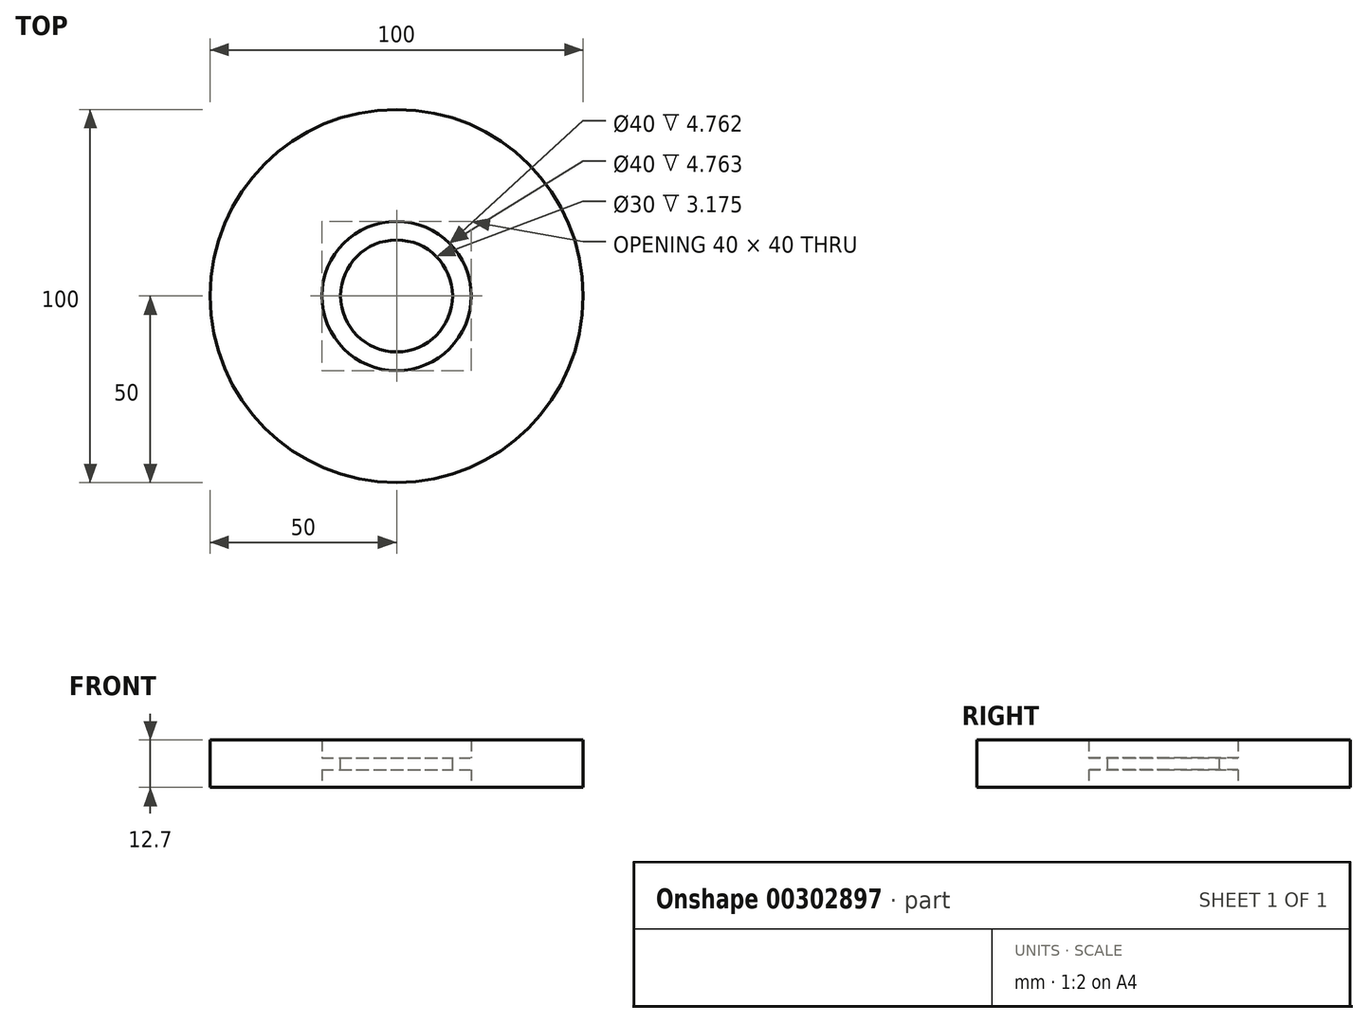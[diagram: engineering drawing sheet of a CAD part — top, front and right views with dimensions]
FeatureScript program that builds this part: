
annotation { "Feature Type Name" : "Feature", "Feature Type Description" : "" }
export const myFeature = defineFeature(function(context is Context, id is Id, definition is map)
    precondition{}
    {
        {
            var Q0;
            Q0=qCreatedBy(makeId("Top.planeOp"),FACE);
            var sketch = newSketch(context, id + "F0", { "sketchPlane" : qUnion([Q0])});
            skCircle(sketch, "E0", {"center": v(0, 0) * mm, "radius": 50 * mm});
            skCircle(sketch, "E1", {"center": v(0, 0) * mm, "radius": 20 * mm});
            skSolve(sketch);
        }
        {
            var Q0;
            Q0=makeQuery(id+"F0.imprint","IMPRINT",FACE,{"disambiguationData":[TD([[makeQuery(id+"F0.imprint","IMPRINT",EDGE,{"derivedFrom":sQuery(id+"F0.wireOp",EDGE,"E0")}),1.0]])]});
            extrude(context, id + "F1", {"entities" : qUnion([Q0]), "depth" : 12.7 * mm});
        }
        {
            var Q0;
            Q0=makeQuery(id+"F1.opExtrude","CAP_FACE",FACE,{"disambiguationData":[OSD([sQuery(id+"F0.wireOp",EDGE,"E0"),sQuery(id+"F0.wireOp",EDGE,"E1")])],"isStart":true});
            var Q1;
            Q1=makeQuery(id+"F1.opExtrude","CAP_FACE",FACE,{"disambiguationData":[OSD([sQuery(id+"F0.wireOp",EDGE,"E0"),sQuery(id+"F0.wireOp",EDGE,"E1")])],"isStart":false});
            cPlane(context, id + "F2", {"entities" : qUnion([Q0, Q1]), "cplaneType" : CPlaneType.MID_PLANE, "offset" : 25.4 * mm, "width" : 152.4 * mm, "height" : 152.4 * mm});
        }
        {
            var Q0;
            Q0=qCreatedBy(id+"F2.planeOp",FACE);
            var sketch = newSketch(context, id + "F3", { "sketchPlane" : qUnion([Q0])});
            skCircle(sketch, "E2", {"center": v(0, 0) * mm, "radius": 20 * mm});
            skCircle(sketch, "E3", {"center": v(0, 0) * mm, "radius": 15 * mm});
            skSolve(sketch);
        }
        {
            var Q0;
            Q0 = qSketchRegion(id + "F3", true);
            extrude(context, id + "F4", {"entities" : qUnion([Q0]), "operationType" : NewBodyOperationType.ADD, "endBound" : BoundingType.SYMMETRIC, "depth" : 3.17 * mm});
        }
    });
